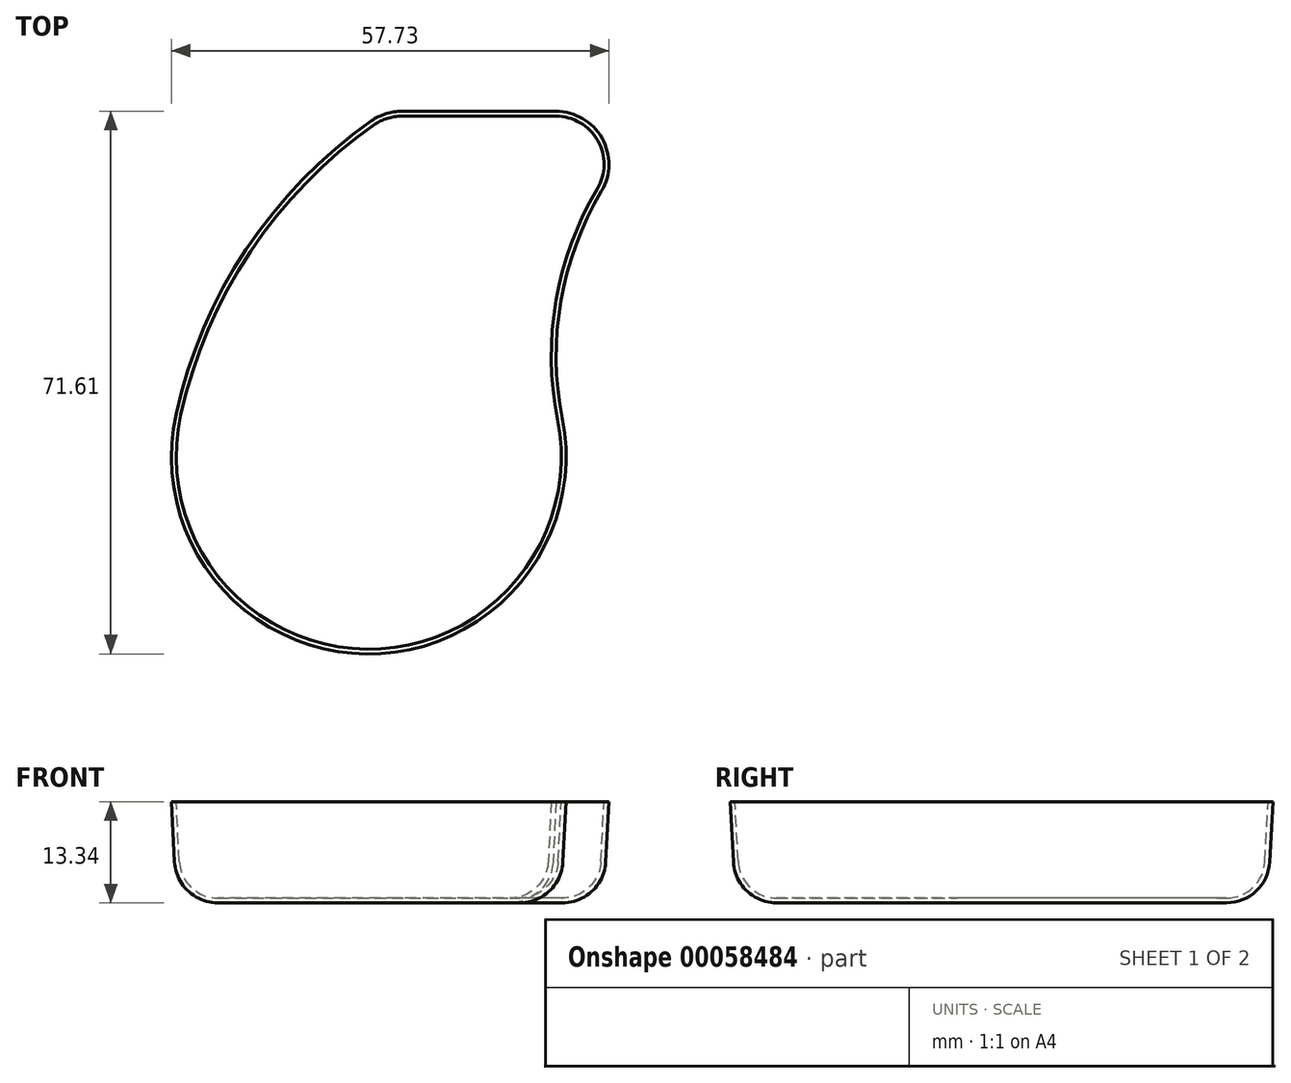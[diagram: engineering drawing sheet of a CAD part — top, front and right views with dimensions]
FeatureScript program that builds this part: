
annotation { "Feature Type Name" : "Feature", "Feature Type Description" : "" }
export const myFeature = defineFeature(function(context is Context, id is Id, definition is map)
    precondition{}
    {
        {
            var Q0;
            Q0=qCreatedBy(makeId("Top.planeOp"),FACE);
            var sketch = newSketch(context, id + "F0", { "sketchPlane" : qUnion([Q0])});
            skArc(sketch, "E0", {"start": v(-24.8, 5.48) * mm, "mid": v(-0.28, -25.4) * mm, "end": v(24.92, 4.94) * mm});
            skLineSegment(sketch, "E1", {"start": v(4.36, 44.94) * mm, "end": v(24.7, 44.94) * mm});
            skArc(sketch, "E2", {"start": v(30.16, 35.34) * mm, "mid": v(24.72, 20.62) * mm, "end": v(24.92, 4.94) * mm});
            skArc(sketch, "E3", {"start": v(0.71, 43.78) * mm, "mid": v(-15.63, 27.02) * mm, "end": v(-24.8, 5.48) * mm});
            skPoint(sketch, "E4.visualSharp", {"position": v(37.93, 44.94) * mm});
            skArc(sketch, "E4.filletArc", {"start": v(30.16, 35.34) * mm, "mid": v(30.22, 41.72) * mm, "end": v(24.7, 44.94) * mm});
            skPoint(sketch, "E5.visualSharp", {"position": v(2.41, 44.94) * mm});
            skArc(sketch, "E5.filletArc", {"start": v(4.36, 44.94) * mm, "mid": v(2.45, 44.64) * mm, "end": v(0.71, 43.78) * mm});
            skSolve(sketch);
        }
        {
            var Q0;
            Q0=makeQuery(id+"F0.imprint","IMPRINT",FACE,{"disambiguationData":[TD([[makeQuery(id+"F0.imprint","IMPRINT",EDGE,{"derivedFrom":sQuery(id+"F0.wireOp",EDGE,"E0")}),1.0]])]});
            extrude(context, id + "F1", {"entities" : qUnion([Q0]), "oppositeDirection" : true, "depth" : 12.7 * mm, "hasDraft" : true, "draftAngle" : 3 * degree, "draftPullDirection" : true});
        }
        {
            var Q0;
            Q0=makeQuery(id+"F1.opExtrude","CAP_EDGE",EDGE,{"disambiguationData":[OSD([sQuery(id+"F0.wireOp",EDGE,"E0")])],"isStart":false});
            fillet(context, id + "F2", {"entities" : qUnion([Q0]), "radius" : 5.08 * mm, "tangentPropagation" : true, "allowEdgeOverflow" : false});
        }
        {
            var Q0;
            Q0=makeQuery(id+"F1.opExtrude","CAP_FACE",FACE,{"disambiguationData":[OSD([sQuery(id+"F0.wireOp",EDGE,"E0"),sQuery(id+"F0.wireOp",EDGE,"E1"),sQuery(id+"F0.wireOp",EDGE,"E2"),sQuery(id+"F0.wireOp",EDGE,"E3"),sQuery(id+"F0.wireOp",EDGE,"E4.filletArc"),sQuery(id+"F0.wireOp",EDGE,"E5.filletArc")])],"isStart":true});
            shell(context, id + "F3", {"entities" : qUnion([Q0]), "thickness" : 0.64 * mm, "oppositeDirection" : true});
        }
    });
